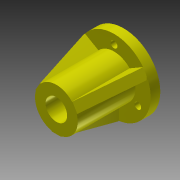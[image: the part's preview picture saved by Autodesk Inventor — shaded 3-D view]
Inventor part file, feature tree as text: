
AUTODESK INVENTOR PART (.ipt)
format: ipt  version: 2013 (Build 170138000, 138)  size: 155,136 bytes
history: native  units: in
note: dims shown in document units (in); Inventor stores cm internally (conversion verified against a paired STEP export)
features: extrude x6, sketch x6, projected_geometry x2, pattern_circular x1
ambient origin geometry x8: Origin, YZ Plane, XZ Plane, XY Plane, X Axis, Y Axis, Z Axis, Center Point
bodies: Solid1 (feature_tree)
feature tree (15):
  extrude  "Extrusion1"  Depth=1.5in
  extrude  "Extrusion2"  Depth=1.125in
  extrude  "Extrusion3"  Depth=0.5625in
  extrude  "Extrusion4"  Depth=0.9843in TaperAngle=0.0deg
  extrude  "Extrusion5"  Depth=0.1969in TaperAngle=0.0deg
  extrude  "Extrusion6"  TaperAngle=0.0deg  [1 undecoded]
  pattern_circular  "Circular Pattern1"  Count=3 Angle=360.0deg
  sketch  "Sketch1"  dims[d0=0.4414in d2=1.5in]
  sketch  "Sketch2"  dims[d3=0.1969in d4=0.0in d5=1.125in]
  sketch  "Sketch3"  dims[d9=1.1811in d10=0.0in d11=0.5625in]
  sketch  "Sketch4"  dims[d12=0.1378in d13=0.9843in d14=0.0in]
  sketch  "Sketch5"  dims[d15=0.1969in d16=0.0in d17=0.1969in d18=0.0in]
  projected_geometry  "Projected Loop1"
  sketch  "Sketch6"  dims[d19=0.25in d20=0.0in d21=0.0in d22=1.1811in d23=360.0deg d26=0.875in]
  projected_geometry  "Project Cut Edges1"
note: 1 required parameter value undecoded (feature->parameter linkage not recoverable at this tier; creation-order binding heuristic only, values carry confidence <= 0.55)
